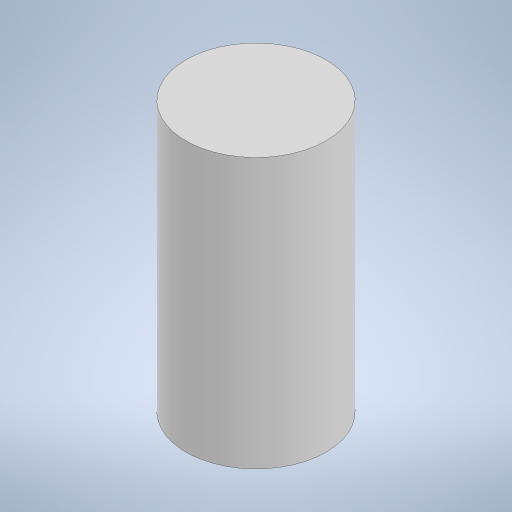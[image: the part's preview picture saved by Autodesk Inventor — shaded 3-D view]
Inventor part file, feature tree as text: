
AUTODESK INVENTOR PART (.ipt)
format: ipt  version: 2023 (Build 270158000, 158)  size: 198,144 bytes
history: native  units: in
note: dims shown in document units (in); Inventor stores cm internally (conversion verified against a paired STEP export)
features: extrude x1, sketch x1
ambient origin geometry x8: Origin, YZ Plane, XZ Plane, XY Plane, X Axis, Y Axis, Z Axis, Center Point
bodies: Solid1 (feature_tree)
feature tree (2):
  extrude  "Extrusion1"  Depth=1.378in TaperAngle=0.0deg
  sketch  "Sketch1"  dims[d0=0.7165in d1=1.378in d2=0.0in]
